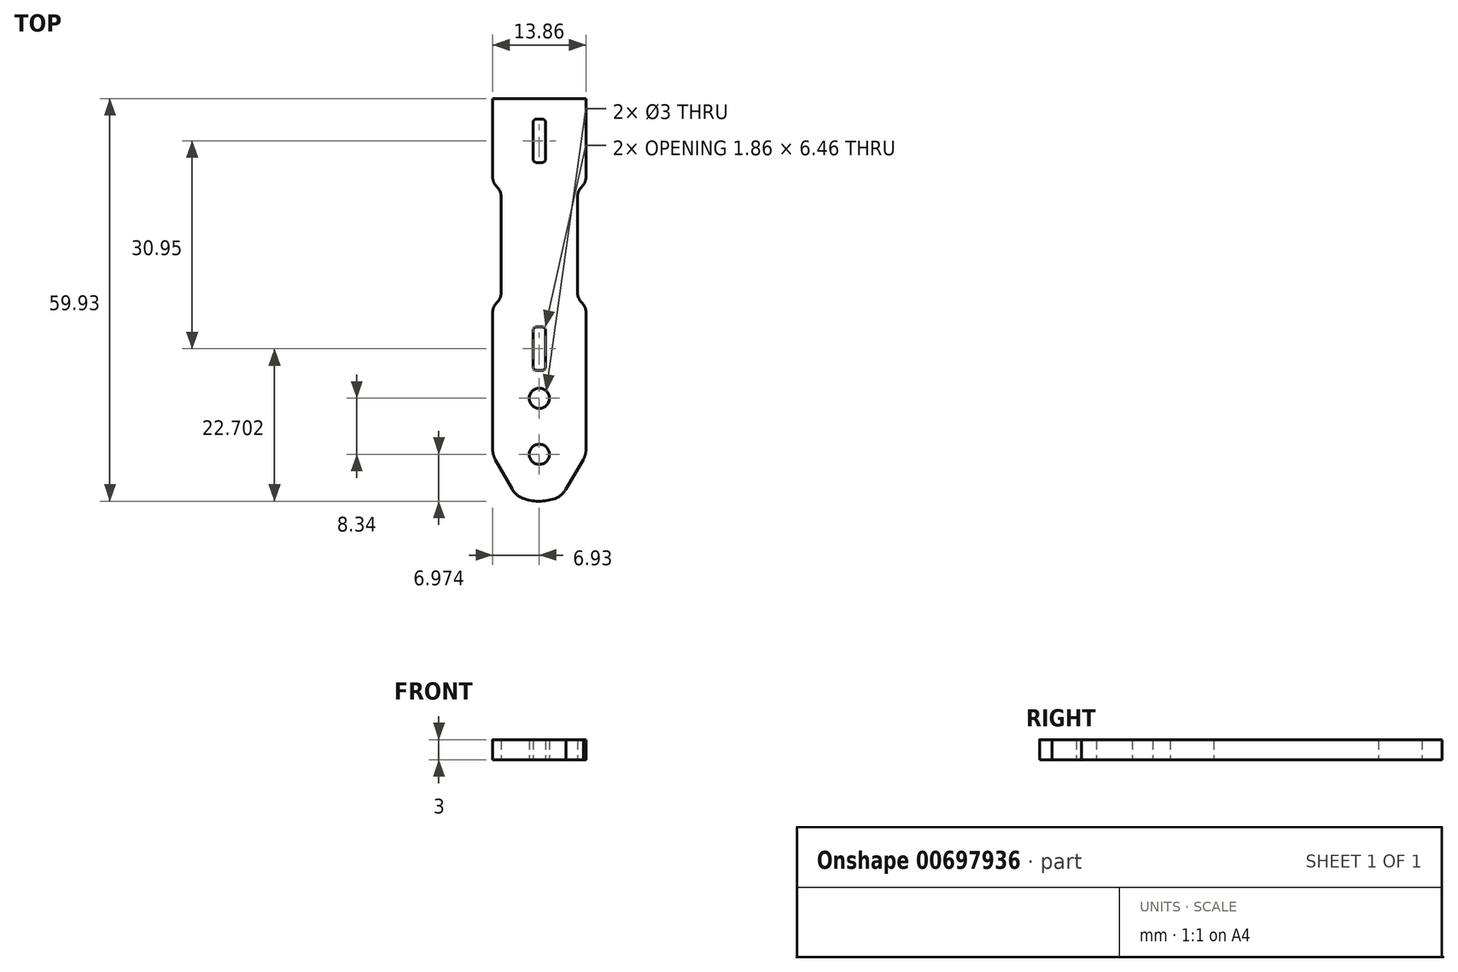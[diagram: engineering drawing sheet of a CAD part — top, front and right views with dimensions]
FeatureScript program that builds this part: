
annotation { "Feature Type Name" : "Feature", "Feature Type Description" : "" }
export const myFeature = defineFeature(function(context is Context, id is Id, definition is map)
    precondition{}
    {
        {
            var Q0;
            Q0=qCreatedBy(makeId("Top.planeOp"),FACE);
            var sketch = newSketch(context, id + "F0", { "sketchPlane" : qUnion([Q0])});
            skLineSegment(sketch, "E0.left", {"start": v(6.93, -37.71) * mm, "end": v(6.93, -35.65) * mm});
            skLineSegment(sketch, "E0.right", {"start": v(-6.93, -37.71) * mm, "end": v(-6.93, -35.65) * mm});
            skLineSegment(sketch, "E1", {"start": v(-6.93, -3.85) * mm, "end": v(6.93, -3.85) * mm});
            skArc(sketch, "E2.MirrorCS", {"start": v(6.93, -56.08) * mm, "mid": v(6.84, -56.84) * mm, "end": v(6.55, -57.55) * mm});
            skArc(sketch, "E3.MirrorCS", {"start": v(-2.48, -63.33) * mm, "mid": v(-3.38, -62.8) * mm, "end": v(-4.05, -61.99) * mm});
            skArc(sketch, "E4.MirrorCS", {"start": v(2.3, -63.4) * mm, "mid": v(-0.1, -63.78) * mm, "end": v(-2.48, -63.33) * mm});
            skLineSegment(sketch, "E5.MirrorCS", {"start": v(-6.55, -57.55) * mm, "end": v(-4.05, -61.99) * mm});
            skCircle(sketch, "E6.MirrorC", {"center": v(0, -56.8) * mm, "radius": 1.5 * mm});
            skLineSegment(sketch, "E7.MirrorCS", {"start": v(6.55, -57.55) * mm, "end": v(3.97, -61.94) * mm});
            skArc(sketch, "E8.MirrorCS", {"start": v(3.97, -61.94) * mm, "mid": v(3.27, -62.83) * mm, "end": v(2.3, -63.4) * mm});
            skCircle(sketch, "E9.MirrorC", {"center": v(0, -48.47) * mm, "radius": 1.5 * mm});
            skPoint(sketch, "E10.MirrorP", {"position": v(-4.43, -35.68) * mm});
            skPoint(sketch, "E11.MirrorP", {"position": v(-8, -56.68) * mm});
            skPoint(sketch, "E12.MirrorP", {"position": v(-4.64, -62.63) * mm});
            skLineSegment(sketch, "E13.MirrorCS", {"start": v(0, -56.8) * mm, "end": v(0, -48.47) * mm, "construction": true});
            skPoint(sketch, "E14.MirrorP", {"position": v(2.23, -62.7) * mm});
            skArc(sketch, "E15.MirrorCS", {"start": v(-6.93, -56.08) * mm, "mid": v(-6.84, -56.84) * mm, "end": v(-6.55, -57.55) * mm});
            skLineSegment(sketch, "E16", {"start": v(-6.93, -56.08) * mm, "end": v(-6.93, -37.71) * mm});
            skLineSegment(sketch, "E17", {"start": v(6.93, -56.08) * mm, "end": v(6.93, -37.71) * mm});
            skLineSegment(sketch, "E18.trimOffspring", {"start": v(-6.93, -15.55) * mm, "end": v(-6.93, -3.85) * mm});
            skLineSegment(sketch, "E19.trimOffspring", {"start": v(6.93, -15.55) * mm, "end": v(6.93, -3.85) * mm});
            skLineSegment(sketch, "E20", {"start": v(-6.34, -34.23) * mm, "end": v(-6.27, -34.17) * mm});
            skLineSegment(sketch, "E21", {"start": v(-6.27, -17.04) * mm, "end": v(-6.34, -16.97) * mm});
            skLineSegment(sketch, "E22.MirrorCS", {"start": v(6.27, -17.04) * mm, "end": v(6.34, -16.97) * mm});
            skLineSegment(sketch, "E23.MirrorCS", {"start": v(6.34, -34.23) * mm, "end": v(6.27, -34.17) * mm});
            skLineSegment(sketch, "E24", {"start": v(-5.68, -18.46) * mm, "end": v(-5.68, -32.75) * mm});
            skLineSegment(sketch, "E25", {"start": v(5.68, -18.46) * mm, "end": v(5.68, -32.75) * mm});
            skPoint(sketch, "E26.MirrorCS.end.orphan", {"position": v(4.43, -18.87) * mm});
            skPoint(sketch, "E26.MirrorCS.start.orphan", {"position": v(4.43, -32.34) * mm});
            skPoint(sketch, "E27.orphan", {"position": v(-4.43, -18.87) * mm});
            skPoint(sketch, "E28.orphan", {"position": v(-4.43, -32.34) * mm});
            skPoint(sketch, "E29.visualSharp", {"position": v(-5.68, -17.63) * mm});
            skArc(sketch, "E29.filletArc", {"start": v(-5.68, -18.46) * mm, "mid": v(-5.84, -17.7) * mm, "end": v(-6.27, -17.04) * mm});
            skPoint(sketch, "E30.visualSharp", {"position": v(-5.68, -33.58) * mm});
            skArc(sketch, "E30.filletArc", {"start": v(-6.27, -34.17) * mm, "mid": v(-5.84, -33.51) * mm, "end": v(-5.68, -32.75) * mm});
            skPoint(sketch, "E31.visualSharp", {"position": v(5.68, -33.58) * mm});
            skArc(sketch, "E31.filletArc", {"start": v(5.68, -32.75) * mm, "mid": v(5.84, -33.51) * mm, "end": v(6.27, -34.17) * mm});
            skPoint(sketch, "E32.visualSharp", {"position": v(5.68, -17.63) * mm});
            skArc(sketch, "E32.filletArc", {"start": v(6.27, -17.04) * mm, "mid": v(5.84, -17.7) * mm, "end": v(5.68, -18.46) * mm});
            skPoint(sketch, "E33.visualSharp", {"position": v(6.93, -16.39) * mm});
            skArc(sketch, "E33.filletArc", {"start": v(6.34, -16.97) * mm, "mid": v(6.78, -16.32) * mm, "end": v(6.93, -15.55) * mm});
            skArc(sketch, "E34.filletArc", {"start": v(-6.93, -15.55) * mm, "mid": v(-6.78, -16.32) * mm, "end": v(-6.34, -16.97) * mm});
            skPoint(sketch, "E35.visualSharp", {"position": v(-6.93, -34.82) * mm});
            skArc(sketch, "E35.filletArc", {"start": v(-6.34, -34.23) * mm, "mid": v(-6.78, -34.88) * mm, "end": v(-6.93, -35.65) * mm});
            skPoint(sketch, "E36.visualSharp", {"position": v(6.93, -34.82) * mm});
            skArc(sketch, "E36.filletArc", {"start": v(6.93, -35.65) * mm, "mid": v(6.78, -34.88) * mm, "end": v(6.34, -34.23) * mm});
            skLineSegment(sketch, "E37.bottom", {"start": v(0.43, -13.36) * mm, "end": v(-0.43, -13.36) * mm});
            skLineSegment(sketch, "E37.top", {"start": v(0.43, -6.9) * mm, "end": v(-0.43, -6.9) * mm});
            skLineSegment(sketch, "E37.left", {"start": v(0.93, -12.86) * mm, "end": v(0.93, -7.4) * mm});
            skLineSegment(sketch, "E37.right", {"start": v(-0.93, -12.86) * mm, "end": v(-0.93, -7.4) * mm});
            skPoint(sketch, "E37.middle", {"position": v(0, -10.13) * mm});
            skPoint(sketch, "E38.startSnap0", {"position": v(0, -13.36) * mm});
            skPoint(sketch, "E39.orphan", {"position": v(0, -27.26) * mm});
            skLineSegment(sketch, "E40", {"start": v(0, -25.6) * mm, "end": v(5.68, -25.6) * mm});
            skPoint(sketch, "E40.startSnap0", {"position": v(5.68, -25.6) * mm});
            skPoint(sketch, "E41.start.orphan", {"position": v(0, -24.33) * mm});
            skPoint(sketch, "E42.MirrorP", {"position": v(0, -41.08) * mm});
            skLineSegment(sketch, "E43.MirrorCS", {"start": v(0.43, -37.85) * mm, "end": v(-0.43, -37.85) * mm});
            skLineSegment(sketch, "E44.MirrorCS", {"start": v(-0.93, -38.35) * mm, "end": v(-0.93, -43.8) * mm});
            skLineSegment(sketch, "E45.MirrorCS", {"start": v(0.43, -44.3) * mm, "end": v(-0.43, -44.3) * mm});
            skLineSegment(sketch, "E46.MirrorCS", {"start": v(0.93, -38.35) * mm, "end": v(0.93, -43.8) * mm});
            skPoint(sketch, "E47.MirrorP", {"position": v(0, -37.85) * mm});
            skPoint(sketch, "E48.visualSharp", {"position": v(-0.93, -6.9) * mm});
            skArc(sketch, "E48.filletArc", {"start": v(-0.43, -6.9) * mm, "mid": v(-0.78, -7.04) * mm, "end": v(-0.93, -7.4) * mm});
            skPoint(sketch, "E49.visualSharp", {"position": v(0.93, -6.9) * mm});
            skArc(sketch, "E49.filletArc", {"start": v(0.93, -7.4) * mm, "mid": v(0.78, -7.04) * mm, "end": v(0.43, -6.9) * mm});
            skPoint(sketch, "E50.visualSharp", {"position": v(0.93, -13.36) * mm});
            skArc(sketch, "E50.filletArc", {"start": v(0.43, -13.36) * mm, "mid": v(0.78, -13.21) * mm, "end": v(0.93, -12.86) * mm});
            skPoint(sketch, "E51.visualSharp", {"position": v(-0.93, -13.36) * mm});
            skArc(sketch, "E51.filletArc", {"start": v(-0.93, -12.86) * mm, "mid": v(-0.78, -13.21) * mm, "end": v(-0.43, -13.36) * mm});
            skPoint(sketch, "E52.visualSharp", {"position": v(-0.93, -37.85) * mm});
            skArc(sketch, "E52.filletArc", {"start": v(-0.43, -37.85) * mm, "mid": v(-0.78, -38) * mm, "end": v(-0.93, -38.35) * mm});
            skPoint(sketch, "E53.visualSharp", {"position": v(0.93, -37.85) * mm});
            skArc(sketch, "E53.filletArc", {"start": v(0.93, -38.35) * mm, "mid": v(0.78, -38) * mm, "end": v(0.43, -37.85) * mm});
            skPoint(sketch, "E54.visualSharp", {"position": v(0.93, -44.3) * mm});
            skArc(sketch, "E54.filletArc", {"start": v(0.43, -44.3) * mm, "mid": v(0.78, -44.16) * mm, "end": v(0.93, -43.8) * mm});
            skPoint(sketch, "E55.visualSharp", {"position": v(-0.93, -44.3) * mm});
            skArc(sketch, "E55.filletArc", {"start": v(-0.93, -43.8) * mm, "mid": v(-0.78, -44.16) * mm, "end": v(-0.43, -44.3) * mm});
            skSolve(sketch);
        }
        {
            var Q0;
            Q0 = qSketchRegion(id + "F0", true);
            extrude(context, id + "F1", {"entities" : qUnion([Q0]), "depth" : 3 * mm, "offsetDistance" : 25 * mm});
        }
    });
